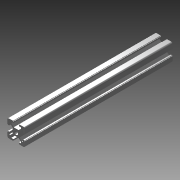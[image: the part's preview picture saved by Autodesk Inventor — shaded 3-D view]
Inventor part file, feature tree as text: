
AUTODESK INVENTOR PART (.ipt)
format: ipt  version: 2015 SP1 (Build 190203100, 203)  size: 155,648 bytes
history: native  units: mm
features: extrude x2, mirror x2, sketch x2, fillet x1
ambient origin geometry x8: Origin, YZ Plane, XZ Plane, XY Plane, X Axis, Y Axis, Z Axis, Center Point
bodies: Solid1 (feature_tree)
feature tree (7):
  extrude  "Extrusion1"  Depth=10.0mm
  fillet  "Fillet1"  Radius=10.0mm
  mirror  "Mirror1"
  mirror  "Mirror2"
  extrude  "Extrusion2"  Depth=6.1mm
  sketch  "Sketch1"  dims[d0=45.0deg d1=5.63mm d2=10.0mm]
  sketch  "Sketch2"  dims[d3=3.1mm d5=6.1mm d6=1.5mm d7=2.0mm d8=170.0mm d9=0.0mm d10=1.5mm d11=3.6mm d12=4.45mm d13=10.0mm d14=0.0mm]
